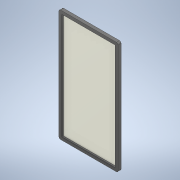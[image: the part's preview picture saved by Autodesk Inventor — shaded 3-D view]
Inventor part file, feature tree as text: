
AUTODESK INVENTOR PART (.ipt)
format: ipt  version: 2020 (Build 240168000, 168)  size: 114,176 bytes
history: native  units: in
note: dims shown in document units (in); Inventor stores cm internally (conversion verified against a paired STEP export)
features: extrude x2, sketch x2, fillet x1
ambient origin geometry x8: Origin, YZ Plane, XZ Plane, XY Plane, X Axis, Y Axis, Z Axis, Center Point
bodies: Solid1 (feature_tree)
feature tree (5):
  extrude  "Extrusion1"  Depth=29.1339in
  extrude  "Extrusion2"  Depth=13.7795in
  fillet  "Fillet1"  Radius=27.5591in
  sketch  "Sketch1"  dims[d0=15.3543in d1=29.1339in]
  sketch  "Sketch2"  dims[d4=0.7874in d5=0.0in d6=13.7795in d7=27.5591in d8=0.3937in d9=0.0in d10=0.3937in]
